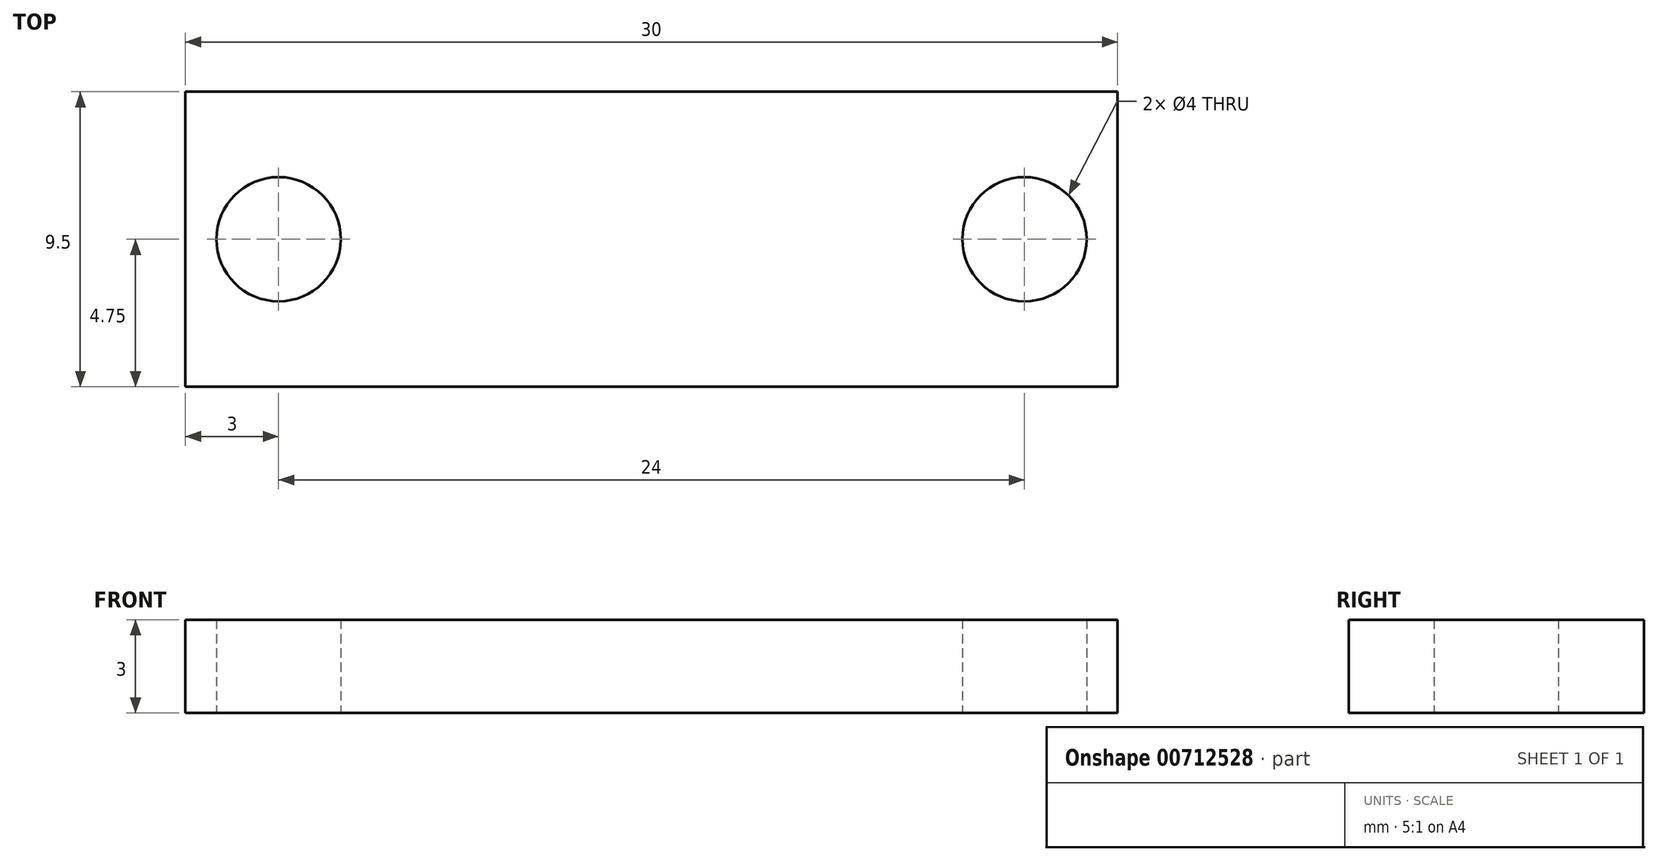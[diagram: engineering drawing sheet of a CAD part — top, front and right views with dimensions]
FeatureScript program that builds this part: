
annotation { "Feature Type Name" : "Feature", "Feature Type Description" : "" }
export const myFeature = defineFeature(function(context is Context, id is Id, definition is map)
    precondition{}
    {
        {
            var Q0;
            Q0=qCreatedBy(makeId("Top.planeOp"),FACE);
            var sketch = newSketch(context, id + "F0", { "sketchPlane" : qUnion([Q0])});
            skLineSegment(sketch, "E0.bottom", {"start": v(15, -4.75) * mm, "end": v(-15, -4.75) * mm});
            skLineSegment(sketch, "E0.top", {"start": v(15, 4.75) * mm, "end": v(-15, 4.75) * mm});
            skLineSegment(sketch, "E0.left", {"start": v(15, -4.75) * mm, "end": v(15, 4.75) * mm});
            skLineSegment(sketch, "E0.right", {"start": v(-15, -4.75) * mm, "end": v(-15, 4.75) * mm});
            skPoint(sketch, "E0.middle", {"position": v(0, 0) * mm});
            skCircle(sketch, "E1", {"center": v(-12, 0) * mm, "radius": 2 * mm});
            skCircle(sketch, "E2", {"center": v(12, 0) * mm, "radius": 2 * mm});
            skSolve(sketch);
        }
        {
            var Q0;
            Q0=makeQuery(id+"F0.imprint","IMPRINT",FACE,{"disambiguationData":[TD([[makeQuery(id+"F0.imprint","IMPRINT",EDGE,{"derivedFrom":sQuery(id+"F0.wireOp",EDGE,"E0.bottom")}),-1.0]])]});
            extrude(context, id + "F1", {"entities" : qUnion([Q0]), "depth" : 3 * mm, "offsetDistance" : 25 * mm});
        }
    });
